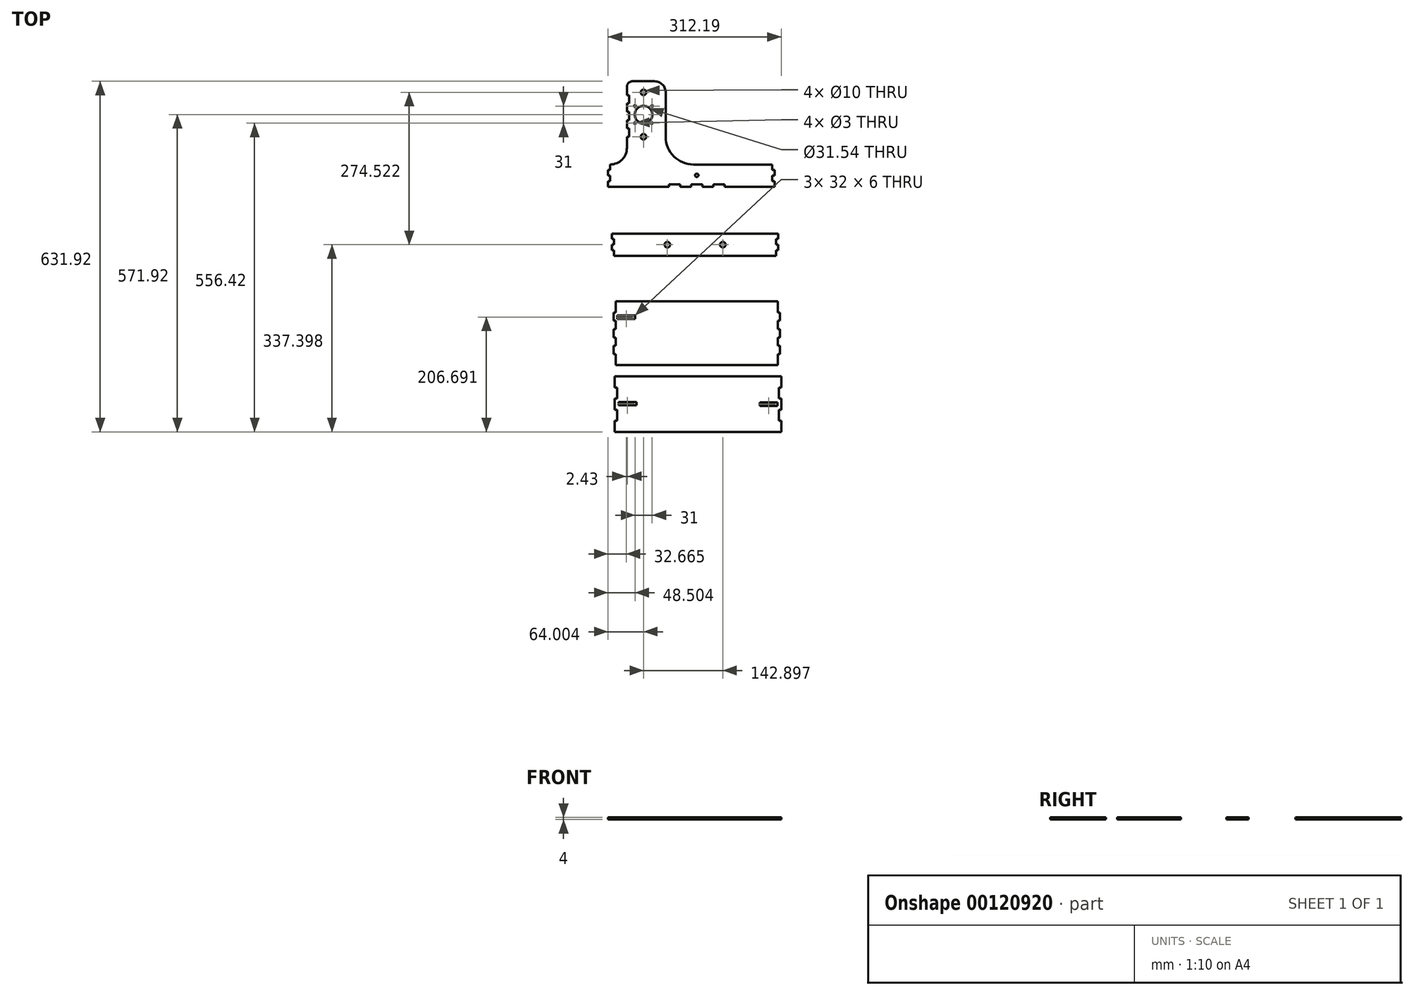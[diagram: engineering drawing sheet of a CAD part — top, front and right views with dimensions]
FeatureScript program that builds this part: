
annotation { "Feature Type Name" : "Feature", "Feature Type Description" : "" }
export const myFeature = defineFeature(function(context is Context, id is Id, definition is map)
    precondition{}
    {
        {
            var Q0;
            Q0=qCreatedBy(makeId("Top.planeOp"),FACE);
            var sketch = newSketch(context, id + "F0", { "sketchPlane" : qUnion([Q0])});
            skLineSegment(sketch, "E0.bottom", {"start": v(-188.26, 10) * mm, "end": v(-188.26, 10) * mm});
            skLineSegment(sketch, "E0.top", {"start": v(-192.26, -30) * mm, "end": v(-82.26, -30) * mm});
            skLineSegment(sketch, "E0.left", {"start": v(-192.26, 0) * mm, "end": v(-192.26, -10) * mm});
            skLineSegment(sketch, "E0.right", {"start": v(107.74, 0) * mm, "end": v(107.74, -10) * mm});
            skLineSegment(sketch, "E1.top", {"start": v(-148.26, 160) * mm, "end": v(-108.26, 160) * mm});
            skLineSegment(sketch, "E1.left", {"start": v(-158.26, 40) * mm, "end": v(-158.26, 60) * mm});
            skLineSegment(sketch, "E1.right", {"start": v(-88.26, 60) * mm, "end": v(-88.26, 140) * mm});
            skLineSegment(sketch, "E2.bottom", {"start": v(-192.26, 0) * mm, "end": v(-188.26, 0) * mm});
            skLineSegment(sketch, "E2.right", {"start": v(-188.26, 0) * mm, "end": v(-188.26, 10) * mm});
            skLineSegment(sketch, "E3.bottom", {"start": v(-192.26, -20) * mm, "end": v(-188.26, -20) * mm});
            skLineSegment(sketch, "E3.top", {"start": v(-192.26, -10) * mm, "end": v(-188.26, -10) * mm});
            skLineSegment(sketch, "E3.right", {"start": v(-188.26, -20) * mm, "end": v(-188.26, -10) * mm});
            skLineSegment(sketch, "E4.trimOffspring", {"start": v(-38.26, 10) * mm, "end": v(103.74, 10) * mm});
            skLineSegment(sketch, "E5.trimOffspring", {"start": v(-192.26, -20) * mm, "end": v(-192.26, -30) * mm});
            skLineSegment(sketch, "E6.bottom", {"start": v(107.74, 0) * mm, "end": v(103.74, 0) * mm});
            skLineSegment(sketch, "E6.right", {"start": v(103.74, 0) * mm, "end": v(103.74, 10) * mm});
            skLineSegment(sketch, "E7.bottom", {"start": v(107.74, -20) * mm, "end": v(103.74, -20) * mm});
            skLineSegment(sketch, "E7.top", {"start": v(107.74, -10) * mm, "end": v(103.74, -10) * mm});
            skLineSegment(sketch, "E7.right", {"start": v(103.74, -20) * mm, "end": v(103.74, -10) * mm});
            skPoint(sketch, "E8.visualSharp", {"position": v(-158.26, 10) * mm});
            skArc(sketch, "E8.filletArc", {"start": v(-188.26, 10) * mm, "mid": v(-167.04, 18.79) * mm, "end": v(-158.26, 40) * mm});
            skPoint(sketch, "E9.visualSharp", {"position": v(-158.26, 160) * mm});
            skArc(sketch, "E9.filletArc", {"start": v(-148.26, 160) * mm, "mid": v(-155.33, 157.07) * mm, "end": v(-158.26, 150) * mm});
            skPoint(sketch, "E10.visualSharp", {"position": v(-88.26, 160) * mm});
            skArc(sketch, "E10.filletArc", {"start": v(-88.26, 140) * mm, "mid": v(-94.11, 154.14) * mm, "end": v(-108.26, 160) * mm});
            skPoint(sketch, "E11.visualSharp", {"position": v(-88.26, 10) * mm});
            skArc(sketch, "E11.filletArc", {"start": v(-88.26, 60) * mm, "mid": v(-73.61, 24.64) * mm, "end": v(-38.26, 10) * mm});
            skLineSegment(sketch, "E12.trimOffspring", {"start": v(107.74, -20) * mm, "end": v(107.74, -30) * mm});
            skCircle(sketch, "E13", {"center": v(-128.26, 140) * mm, "radius": 5 * mm});
            skPoint(sketch, "E13.centerSnap0", {"position": v(-128.26, 160) * mm});
            skCircle(sketch, "E14", {"center": v(-128.26, 60) * mm, "radius": 5 * mm});
            skLineSegment(sketch, "E15.bottom", {"start": v(-158.26, 60) * mm, "end": v(-154.26, 60) * mm});
            skLineSegment(sketch, "E15.top", {"start": v(-158.26, 75) * mm, "end": v(-154.26, 75) * mm});
            skLineSegment(sketch, "E15.right", {"start": v(-154.26, 89.1) * mm, "end": v(-154.26, 104.1) * mm});
            skLineSegment(sketch, "E16.bottom", {"start": v(-158.26, 90) * mm, "end": v(-154.26, 90) * mm});
            skLineSegment(sketch, "E16.top", {"start": v(-158.26, 105) * mm, "end": v(-154.26, 105) * mm});
            skLineSegment(sketch, "E16.right", {"start": v(-154.26, 90) * mm, "end": v(-154.26, 105) * mm});
            skLineSegment(sketch, "E17.bottom", {"start": v(-158.26, 120) * mm, "end": v(-154.26, 120) * mm});
            skLineSegment(sketch, "E17.top", {"start": v(-158.26, 135) * mm, "end": v(-154.26, 135) * mm});
            skLineSegment(sketch, "E17.right", {"start": v(-154.26, 120) * mm, "end": v(-154.26, 135) * mm});
            skLineSegment(sketch, "E18.trimOffspring", {"start": v(-158.26, 75) * mm, "end": v(-158.26, 90) * mm});
            skLineSegment(sketch, "E19.trimOffspring", {"start": v(-158.26, 105) * mm, "end": v(-158.26, 120) * mm});
            skLineSegment(sketch, "E20.trimOffspring", {"start": v(-158.26, 135) * mm, "end": v(-158.26, 150) * mm});
            skLineSegment(sketch, "E21.top", {"start": v(-181.36, -154.52) * mm, "end": v(110.64, -154.52) * mm});
            skLineSegment(sketch, "E21.left", {"start": v(-185.36, -114.52) * mm, "end": v(-185.36, -124.52) * mm});
            skLineSegment(sketch, "E21.right", {"start": v(114.64, -114.52) * mm, "end": v(114.64, -124.52) * mm});
            skLineSegment(sketch, "E22.bottom", {"start": v(-185.36, -124.52) * mm, "end": v(-181.36, -124.52) * mm});
            skLineSegment(sketch, "E22.left", {"start": v(-185.36, -124.52) * mm, "end": v(-185.36, -110.78) * mm});
            skLineSegment(sketch, "E23.bottom", {"start": v(-185.36, -144.52) * mm, "end": v(-181.36, -144.52) * mm});
            skLineSegment(sketch, "E23.top", {"start": v(-185.36, -134.52) * mm, "end": v(-181.36, -134.52) * mm});
            skLineSegment(sketch, "E23.left", {"start": v(-185.36, -144.52) * mm, "end": v(-185.36, -134.52) * mm});
            skLineSegment(sketch, "E24.trimOffspring", {"start": v(-185.36, -134.52) * mm, "end": v(-185.36, -144.52) * mm});
            skLineSegment(sketch, "E25", {"start": v(-181.36, -144.52) * mm, "end": v(-181.36, -154.52) * mm});
            skLineSegment(sketch, "E26", {"start": v(-185.36, -114.52) * mm, "end": v(114.64, -114.52) * mm});
            skLineSegment(sketch, "E27", {"start": v(-181.36, -124.52) * mm, "end": v(-181.36, -134.52) * mm});
            skLineSegment(sketch, "E28.bottom", {"start": v(114.64, -124.52) * mm, "end": v(110.64, -124.52) * mm});
            skLineSegment(sketch, "E28.top", {"start": v(114.64, -134.52) * mm, "end": v(110.64, -134.52) * mm});
            skLineSegment(sketch, "E28.right", {"start": v(110.64, -124.52) * mm, "end": v(110.64, -134.52) * mm});
            skLineSegment(sketch, "E29.top", {"start": v(114.64, -144.52) * mm, "end": v(110.64, -144.52) * mm});
            skLineSegment(sketch, "E29.right", {"start": v(110.64, -154.52) * mm, "end": v(110.64, -144.52) * mm});
            skLineSegment(sketch, "E30.trimOffspring", {"start": v(114.64, -134.52) * mm, "end": v(114.64, -144.52) * mm});
            skCircle(sketch, "E31", {"center": v(-85.36, -134.52) * mm, "radius": 5 * mm});
            skCircle(sketch, "E32", {"center": v(14.64, -134.52) * mm, "radius": 5 * mm});
            skCircle(sketch, "E33", {"center": v(-128.26, 100) * mm, "radius": 15.77 * mm});
            skCircle(sketch, "E34", {"center": v(-112.76, 115.5) * mm, "radius": 1.5 * mm});
            skCircle(sketch, "E35", {"center": v(-143.76, 115.5) * mm, "radius": 1.5 * mm});
            skCircle(sketch, "E36", {"center": v(-143.76, 84.5) * mm, "radius": 1.5 * mm});
            skCircle(sketch, "E37", {"center": v(-113.35, 84.5) * mm, "radius": 1.5 * mm});
            skLineSegment(sketch, "E38.bottom", {"start": v(-178.5, -236.78) * mm, "end": v(113.5, -236.78) * mm});
            skLineSegment(sketch, "E38.top", {"start": v(-178.5, -351.78) * mm, "end": v(113.5, -351.78) * mm});
            skLineSegment(sketch, "E38.left", {"start": v(-182.5, -256.78) * mm, "end": v(-182.5, -271.78) * mm});
            skLineSegment(sketch, "E38.right", {"start": v(117.5, -256.78) * mm, "end": v(117.5, -271.78) * mm});
            skLineSegment(sketch, "E39.top", {"start": v(-178.5, -256.78) * mm, "end": v(-182.5, -256.78) * mm});
            skLineSegment(sketch, "E39.left", {"start": v(-178.5, -236.78) * mm, "end": v(-178.5, -256.78) * mm});
            skPoint(sketch, "E40.firstSnap0", {"position": v(-178.5, -246.78) * mm});
            skLineSegment(sketch, "E40.top", {"start": v(-178.5, -331.78) * mm, "end": v(-182.5, -331.78) * mm});
            skLineSegment(sketch, "E40.left", {"start": v(-178.5, -351.78) * mm, "end": v(-178.5, -331.78) * mm});
            skLineSegment(sketch, "E41.bottom", {"start": v(-182.5, -271.78) * mm, "end": v(-178.5, -271.78) * mm});
            skLineSegment(sketch, "E41.top", {"start": v(-182.5, -286.78) * mm, "end": v(-178.5, -286.78) * mm});
            skLineSegment(sketch, "E41.right", {"start": v(-178.5, -271.78) * mm, "end": v(-178.5, -286.78) * mm});
            skLineSegment(sketch, "E42.bottom", {"start": v(-182.5, -301.78) * mm, "end": v(-178.5, -301.78) * mm});
            skLineSegment(sketch, "E42.top", {"start": v(-182.5, -316.78) * mm, "end": v(-178.5, -316.78) * mm});
            skLineSegment(sketch, "E42.right", {"start": v(-178.5, -301.78) * mm, "end": v(-178.5, -316.78) * mm});
            skLineSegment(sketch, "E43.trimOffspring", {"start": v(-182.5, -316.78) * mm, "end": v(-182.5, -331.78) * mm});
            skLineSegment(sketch, "E44.trimOffspring", {"start": v(-182.5, -286.78) * mm, "end": v(-182.5, -301.78) * mm});
            skLineSegment(sketch, "E45.top", {"start": v(117.5, -331.78) * mm, "end": v(113.5, -331.78) * mm});
            skLineSegment(sketch, "E45.right", {"start": v(113.5, -351.78) * mm, "end": v(113.5, -331.78) * mm});
            skLineSegment(sketch, "E46.bottom", {"start": v(117.5, -316.78) * mm, "end": v(113.5, -316.78) * mm});
            skLineSegment(sketch, "E46.top", {"start": v(117.5, -301.78) * mm, "end": v(113.5, -301.78) * mm});
            skLineSegment(sketch, "E46.right", {"start": v(113.5, -316.78) * mm, "end": v(113.5, -301.78) * mm});
            skLineSegment(sketch, "E47.bottom", {"start": v(117.5, -286.78) * mm, "end": v(113.5, -286.78) * mm});
            skLineSegment(sketch, "E47.top", {"start": v(117.5, -271.78) * mm, "end": v(113.5, -271.78) * mm});
            skLineSegment(sketch, "E47.right", {"start": v(113.5, -286.78) * mm, "end": v(113.5, -271.78) * mm});
            skLineSegment(sketch, "E48.top", {"start": v(117.5, -256.78) * mm, "end": v(113.5, -256.78) * mm});
            skLineSegment(sketch, "E48.right", {"start": v(113.5, -236.78) * mm, "end": v(113.5, -256.78) * mm});
            skLineSegment(sketch, "E49.trimOffspring", {"start": v(117.5, -286.78) * mm, "end": v(117.5, -301.78) * mm});
            skLineSegment(sketch, "E50.trimOffspring", {"start": v(117.5, -316.78) * mm, "end": v(117.5, -331.78) * mm});
            skLineSegment(sketch, "E51.top", {"start": v(-82.26, -26) * mm, "end": v(-62.26, -26) * mm});
            skLineSegment(sketch, "E51.left", {"start": v(-82.26, -30) * mm, "end": v(-82.26, -26) * mm});
            skLineSegment(sketch, "E51.right", {"start": v(-62.26, -30) * mm, "end": v(-62.26, -26) * mm});
            skLineSegment(sketch, "E52.top", {"start": v(-42.26, -26) * mm, "end": v(-22.26, -26) * mm});
            skLineSegment(sketch, "E52.left", {"start": v(-42.26, -30) * mm, "end": v(-42.26, -26) * mm});
            skLineSegment(sketch, "E52.right", {"start": v(-22.26, -30) * mm, "end": v(-22.26, -26) * mm});
            skLineSegment(sketch, "E53.top", {"start": v(-2.26, -26) * mm, "end": v(17.74, -26) * mm});
            skLineSegment(sketch, "E53.left", {"start": v(-2.26, -30) * mm, "end": v(-2.26, -26) * mm});
            skLineSegment(sketch, "E53.right", {"start": v(17.74, -30) * mm, "end": v(17.74, -26) * mm});
            skLineSegment(sketch, "E54.trimOffspring", {"start": v(-62.26, -30) * mm, "end": v(-42.26, -30) * mm});
            skLineSegment(sketch, "E55.trimOffspring", {"start": v(-22.26, -30) * mm, "end": v(-2.26, -30) * mm});
            skLineSegment(sketch, "E56.trimOffspring", {"start": v(17.74, -30) * mm, "end": v(107.74, -30) * mm});
            skLineSegment(sketch, "E57.bottom", {"start": v(-180.07, -371.92) * mm, "end": v(119.93, -371.92) * mm});
            skLineSegment(sketch, "E57.top", {"start": v(-180.07, -471.92) * mm, "end": v(119.93, -471.92) * mm});
            skLineSegment(sketch, "E57.left", {"start": v(-180.07, -371.92) * mm, "end": v(-180.07, -391.92) * mm});
            skLineSegment(sketch, "E57.right", {"start": v(119.93, -371.92) * mm, "end": v(119.93, -391.92) * mm});
            skLineSegment(sketch, "E58.bottom", {"start": v(-180.07, -391.92) * mm, "end": v(-176.07, -391.92) * mm});
            skLineSegment(sketch, "E58.top", {"start": v(-180.07, -411.92) * mm, "end": v(-176.07, -411.92) * mm});
            skLineSegment(sketch, "E58.right", {"start": v(-176.07, -391.92) * mm, "end": v(-176.07, -411.92) * mm});
            skLineSegment(sketch, "E59.bottom", {"start": v(-180.07, -431.92) * mm, "end": v(-176.07, -431.92) * mm});
            skLineSegment(sketch, "E59.top", {"start": v(-180.07, -451.92) * mm, "end": v(-176.07, -451.92) * mm});
            skLineSegment(sketch, "E59.right", {"start": v(-176.07, -431.92) * mm, "end": v(-176.07, -451.92) * mm});
            skLineSegment(sketch, "E60.trimOffspring", {"start": v(-180.07, -411.92) * mm, "end": v(-180.07, -431.92) * mm});
            skLineSegment(sketch, "E61.trimOffspring", {"start": v(-180.07, -451.92) * mm, "end": v(-180.07, -471.92) * mm});
            skLineSegment(sketch, "E62.bottom", {"start": v(119.93, -391.92) * mm, "end": v(115.93, -391.92) * mm});
            skLineSegment(sketch, "E62.top", {"start": v(119.93, -411.92) * mm, "end": v(115.93, -411.92) * mm});
            skLineSegment(sketch, "E62.right", {"start": v(115.93, -391.92) * mm, "end": v(115.93, -411.92) * mm});
            skLineSegment(sketch, "E63.bottom", {"start": v(119.93, -451.92) * mm, "end": v(115.93, -451.92) * mm});
            skLineSegment(sketch, "E63.top", {"start": v(119.93, -431.92) * mm, "end": v(115.93, -431.92) * mm});
            skLineSegment(sketch, "E63.right", {"start": v(115.93, -451.92) * mm, "end": v(115.93, -431.92) * mm});
            skLineSegment(sketch, "E64.trimOffspring", {"start": v(119.93, -411.92) * mm, "end": v(119.93, -431.92) * mm});
            skLineSegment(sketch, "E65.trimOffspring", {"start": v(119.93, -451.92) * mm, "end": v(119.93, -471.92) * mm});
            skCircle(sketch, "E66", {"center": v(-172.06, 206.48) * mm, "radius": 11 * mm});
            skCircle(sketch, "E67", {"center": v(-156.56, 226.48) * mm, "radius": 2 * mm});
            skCircle(sketch, "E68", {"center": v(-187.56, 226.48) * mm, "radius": 2 * mm});
            skCircle(sketch, "E69", {"center": v(-187.56, 186.48) * mm, "radius": 2 * mm});
            skCircle(sketch, "E70", {"center": v(-157.16, 186.48) * mm, "radius": 2 * mm});
            skLineSegment(sketch, "E71.bottom", {"start": v(-148.92, 181.48) * mm, "end": v(-193.92, 181.48) * mm});
            skLineSegment(sketch, "E71.top", {"start": v(-148.92, 231.48) * mm, "end": v(-193.92, 231.48) * mm});
            skLineSegment(sketch, "E71.left", {"start": v(-148.92, 181.48) * mm, "end": v(-148.92, 231.48) * mm});
            skLineSegment(sketch, "E71.right", {"start": v(-193.92, 181.48) * mm, "end": v(-193.92, 231.48) * mm});
            skLineSegment(sketch, "E72.bottom", {"start": v(113.03, -418.92) * mm, "end": v(81.03, -418.92) * mm});
            skLineSegment(sketch, "E72.top", {"start": v(113.03, -424.92) * mm, "end": v(81.03, -424.92) * mm});
            skLineSegment(sketch, "E72.left", {"start": v(113.03, -418.92) * mm, "end": v(113.03, -424.92) * mm});
            skLineSegment(sketch, "E72.right", {"start": v(81.03, -418.92) * mm, "end": v(81.03, -424.92) * mm});
            skLineSegment(sketch, "E73.bottom", {"start": v(-143.6, -262.23) * mm, "end": v(-175.6, -262.23) * mm});
            skLineSegment(sketch, "E73.top", {"start": v(-143.6, -268.23) * mm, "end": v(-175.6, -268.23) * mm});
            skLineSegment(sketch, "E73.left", {"start": v(-143.6, -262.23) * mm, "end": v(-143.6, -268.23) * mm});
            skLineSegment(sketch, "E73.right", {"start": v(-175.6, -262.23) * mm, "end": v(-175.6, -268.23) * mm});
            skCircle(sketch, "E74", {"center": v(-32.26, -9.42) * mm, "radius": 3 * mm});
            skLineSegment(sketch, "E75.bottom", {"start": v(-141.17, -418.1) * mm, "end": v(-173.17, -418.1) * mm});
            skLineSegment(sketch, "E75.top", {"start": v(-141.17, -424.1) * mm, "end": v(-173.17, -424.1) * mm});
            skLineSegment(sketch, "E75.left", {"start": v(-141.17, -418.1) * mm, "end": v(-141.17, -424.1) * mm});
            skLineSegment(sketch, "E75.right", {"start": v(-173.17, -418.1) * mm, "end": v(-173.17, -424.1) * mm});
            skLineSegment(sketch, "E76", {"start": v(-154.26, 60) * mm, "end": v(-154.26, 75) * mm});
            skSolve(sketch);
        }
        {
            var Q0;
            Q0=makeQuery(id+"F0.imprint","IMPRINT",FACE,{"disambiguationData":[TD([[makeQuery(id+"F0.imprint","IMPRINT",EDGE,{"derivedFrom":sQuery(id+"F0.wireOp",EDGE,"E57.bottom")}),-1.0]])]});
            var Q1;
            Q1=makeQuery(id+"F0.imprint","IMPRINT",FACE,{"disambiguationData":[TD([[makeQuery(id+"F0.imprint","IMPRINT",EDGE,{"derivedFrom":sQuery(id+"F0.wireOp",EDGE,"E38.bottom")}),-1.0]])]});
            var Q2;
            Q2=makeQuery(id+"F0.imprint","IMPRINT",FACE,{"disambiguationData":[TD([[makeQuery(id+"F0.imprint","IMPRINT",EDGE,{"derivedFrom":sQuery(id+"F0.wireOp",EDGE,"E21.top")}),1.0]])]});
            var Q3;
            Q3=makeQuery(id+"F0.imprint","IMPRINT",FACE,{"disambiguationData":[TD([[makeQuery(id+"F0.imprint","IMPRINT",EDGE,{"derivedFrom":sQuery(id+"F0.wireOp",EDGE,"E0.top")}),1.0]])]});
            extrude(context, id + "F1", {"entities" : qUnion([Q0, Q1, Q2, Q3]), "depth" : 4 * mm});
        }
    });
